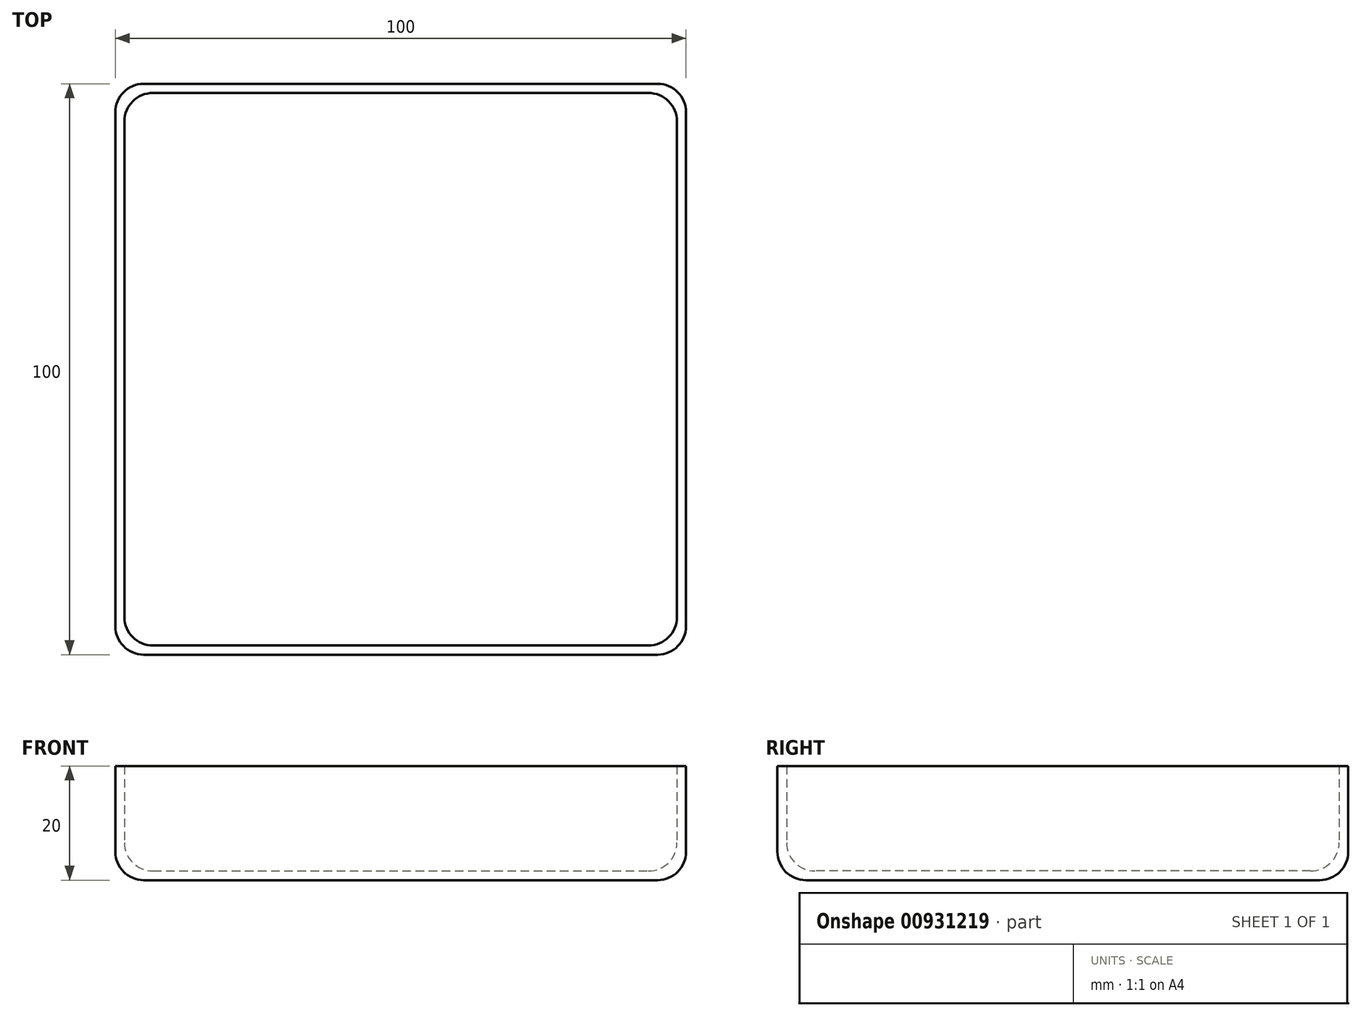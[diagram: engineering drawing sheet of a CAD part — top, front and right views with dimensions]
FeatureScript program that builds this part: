
annotation { "Feature Type Name" : "Feature", "Feature Type Description" : "" }
export const myFeature = defineFeature(function(context is Context, id is Id, definition is map)
    precondition{}
    {
        {
            var Q0;
            Q0=qCreatedBy(makeId("Top.planeOp"),FACE);
            var sketch = newSketch(context, id + "F0", { "sketchPlane" : qUnion([Q0])});
            skLineSegment(sketch, "E0.bottom", {"start": v(-50, 50) * mm, "end": v(50, 50) * mm});
            skLineSegment(sketch, "E0.top", {"start": v(-50, -50) * mm, "end": v(50, -50) * mm});
            skLineSegment(sketch, "E0.left", {"start": v(-50, 50) * mm, "end": v(-50, -50) * mm});
            skLineSegment(sketch, "E0.right", {"start": v(50, 50) * mm, "end": v(50, -50) * mm});
            skPoint(sketch, "E0.middle", {"position": v(0, 0) * mm});
            skSolve(sketch);
        }
        {
            var Q0;
            Q0 = qSketchRegion(id + "F0", true);
            extrude(context, id + "F1", {"entities" : qUnion([Q0]), "depth" : 20 * mm, "offsetDistance" : 25 * mm});
        }
        {
            var Q0;
            Q0=makeQuery(id+"F1.opExtrude","CAP_FACE",FACE,{"disambiguationData":[OSD([sQuery(id+"F0.wireOp",EDGE,"E0.bottom"),sQuery(id+"F0.wireOp",EDGE,"E0.top"),sQuery(id+"F0.wireOp",EDGE,"E0.left"),sQuery(id+"F0.wireOp",EDGE,"E0.right")])],"isStart":false});
            shell(context, id + "F2", {"entities" : qUnion([Q0]), "thickness" : 1.6 * mm});
        }
        {
            var Q0;
            {var subQ0=sQuery(id+"F0.wireOp",EDGE,"E0.left");Q0=makeQuery(id+"F2.opShell","OFFSET_EDGE",EDGE,{"disambiguationData":[OSD([subQ0]),TDD([makeQuery(id+"F1.opExtrude","CAP_EDGE",EDGE,{"disambiguationData":[OSD([subQ0])],"isStart":true})])]});}
            var Q1;
            {var subQ0=sQuery(id+"F0.wireOp",EDGE,"E0.bottom");Q1=makeQuery(id+"F2.opShell","OFFSET_EDGE",EDGE,{"disambiguationData":[OSD([subQ0]),TDD([makeQuery(id+"F1.opExtrude","CAP_EDGE",EDGE,{"disambiguationData":[OSD([subQ0])],"isStart":true})])]});}
            var Q2;
            {var subQ0=sQuery(id+"F0.wireOp",EDGE,"E0.right");Q2=makeQuery(id+"F2.opShell","OFFSET_EDGE",EDGE,{"disambiguationData":[OSD([subQ0]),TDD([makeQuery(id+"F1.opExtrude","CAP_EDGE",EDGE,{"disambiguationData":[OSD([subQ0])],"isStart":true})])]});}
            var Q3;
            {var subQ0=sQuery(id+"F0.wireOp",EDGE,"E0.top");Q3=makeQuery(id+"F2.opShell","OFFSET_EDGE",EDGE,{"disambiguationData":[OSD([subQ0]),TDD([makeQuery(id+"F1.opExtrude","CAP_EDGE",EDGE,{"disambiguationData":[OSD([subQ0])],"isStart":true})])]});}
            fillet(context, id + "F3", {"entities" : qUnion([Q0, Q1, Q2, Q3]), "radius" : 5 * mm, "tangentPropagation" : true, "allowEdgeOverflow" : false});
        }
        {
            var Q0;
            Q0=makeQuery(id+"F2.opShell","OFFSET_EDGE",EDGE,{"disambiguationData":[OSD([sQuery(id+"F0.wireOp",EDGE,"E0.bottom"),sQuery(id+"F0.wireOp",EDGE,"E0.right")])]});
            var Q1;
            {var subQ0=sQuery(id+"F0.wireOp",EDGE,"E0.right");var subQ1=sQuery(id+"F0.wireOp",EDGE,"E0.bottom");Q1=makeQuery(id+"F3.opFillet","BLEND_EDGE",EDGE,{"blendedFrom":[makeQuery(id+"F2.opShell","OFFSET_EDGE",EDGE,{"disambiguationData":[OSD([subQ1]),TDD([makeQuery(id+"F1.opExtrude","CAP_EDGE",EDGE,{"disambiguationData":[OSD([subQ1])],"isStart":true})])]}),makeQuery(id+"F2.opShell","OFFSET_EDGE",EDGE,{"disambiguationData":[OSD([subQ0]),TDD([makeQuery(id+"F1.opExtrude","CAP_EDGE",EDGE,{"disambiguationData":[OSD([subQ0])],"isStart":true})])]})],"blendedInto":[]});}
            var Q2;
            {var subQ0=sQuery(id+"F0.wireOp",EDGE,"E0.right");var subQ1=sQuery(id+"F0.wireOp",EDGE,"E0.top");Q2=makeQuery(id+"F3.opFillet","BLEND_EDGE",EDGE,{"blendedFrom":[makeQuery(id+"F2.opShell","OFFSET_EDGE",EDGE,{"disambiguationData":[OSD([subQ1]),TDD([makeQuery(id+"F1.opExtrude","CAP_EDGE",EDGE,{"disambiguationData":[OSD([subQ1])],"isStart":true})])]}),makeQuery(id+"F2.opShell","OFFSET_EDGE",EDGE,{"disambiguationData":[OSD([subQ0]),TDD([makeQuery(id+"F1.opExtrude","CAP_EDGE",EDGE,{"disambiguationData":[OSD([subQ0])],"isStart":true})])]})],"blendedInto":[]});}
            var Q3;
            Q3=makeQuery(id+"F2.opShell","OFFSET_EDGE",EDGE,{"disambiguationData":[OSD([sQuery(id+"F0.wireOp",EDGE,"E0.top"),sQuery(id+"F0.wireOp",EDGE,"E0.right")])]});
            var Q4;
            {var subQ0=sQuery(id+"F0.wireOp",EDGE,"E0.left");var subQ1=sQuery(id+"F0.wireOp",EDGE,"E0.top");Q4=makeQuery(id+"F3.opFillet","BLEND_EDGE",EDGE,{"blendedFrom":[makeQuery(id+"F2.opShell","OFFSET_EDGE",EDGE,{"disambiguationData":[OSD([subQ1]),TDD([makeQuery(id+"F1.opExtrude","CAP_EDGE",EDGE,{"disambiguationData":[OSD([subQ1])],"isStart":true})])]}),makeQuery(id+"F2.opShell","OFFSET_EDGE",EDGE,{"disambiguationData":[OSD([subQ0]),TDD([makeQuery(id+"F1.opExtrude","CAP_EDGE",EDGE,{"disambiguationData":[OSD([subQ0])],"isStart":true})])]})],"blendedInto":[]});}
            var Q5;
            Q5=makeQuery(id+"F2.opShell","OFFSET_EDGE",EDGE,{"disambiguationData":[OSD([sQuery(id+"F0.wireOp",EDGE,"E0.top"),sQuery(id+"F0.wireOp",EDGE,"E0.left")])]});
            var Q6;
            Q6=makeQuery(id+"F2.opShell","OFFSET_EDGE",EDGE,{"disambiguationData":[OSD([sQuery(id+"F0.wireOp",EDGE,"E0.bottom"),sQuery(id+"F0.wireOp",EDGE,"E0.left")])]});
            var Q7;
            {var subQ0=sQuery(id+"F0.wireOp",EDGE,"E0.left");var subQ1=sQuery(id+"F0.wireOp",EDGE,"E0.bottom");Q7=makeQuery(id+"F3.opFillet","BLEND_EDGE",EDGE,{"blendedFrom":[makeQuery(id+"F2.opShell","OFFSET_EDGE",EDGE,{"disambiguationData":[OSD([subQ1]),TDD([makeQuery(id+"F1.opExtrude","CAP_EDGE",EDGE,{"disambiguationData":[OSD([subQ1])],"isStart":true})])]}),makeQuery(id+"F2.opShell","OFFSET_EDGE",EDGE,{"disambiguationData":[OSD([subQ0]),TDD([makeQuery(id+"F1.opExtrude","CAP_EDGE",EDGE,{"disambiguationData":[OSD([subQ0])],"isStart":true})])]})],"blendedInto":[]});}
            fillet(context, id + "F4", {"entities" : qUnion([Q0, Q1, Q2, Q3, Q4, Q5, Q6, Q7]), "radius" : 5 * mm, "tangentPropagation" : true, "allowEdgeOverflow" : false});
        }
        {
            var Q0;
            Q0=makeQuery(id+"F1.opExtrude","SWEPT_EDGE",EDGE,{"disambiguationData":[OSD([sQuery(id+"F0.wireOp",EDGE,"E0.top"),sQuery(id+"F0.wireOp",EDGE,"E0.right")])]});
            var Q1;
            Q1=makeQuery(id+"F1.opExtrude","SWEPT_EDGE",EDGE,{"disambiguationData":[OSD([sQuery(id+"F0.wireOp",EDGE,"E0.top"),sQuery(id+"F0.wireOp",EDGE,"E0.left")])]});
            var Q2;
            Q2=makeQuery(id+"F1.opExtrude","SWEPT_EDGE",EDGE,{"disambiguationData":[OSD([sQuery(id+"F0.wireOp",EDGE,"E0.bottom"),sQuery(id+"F0.wireOp",EDGE,"E0.left")])]});
            var Q3;
            Q3=makeQuery(id+"F1.opExtrude","SWEPT_EDGE",EDGE,{"disambiguationData":[OSD([sQuery(id+"F0.wireOp",EDGE,"E0.bottom"),sQuery(id+"F0.wireOp",EDGE,"E0.right")])]});
            fillet(context, id + "F5", {"entities" : qUnion([Q0, Q1, Q2, Q3]), "radius" : 5 * mm, "tangentPropagation" : true, "allowEdgeOverflow" : false});
        }
        {
            var Q0;
            Q0=makeQuery(id+"F1.opExtrude","CAP_EDGE",EDGE,{"disambiguationData":[OSD([sQuery(id+"F0.wireOp",EDGE,"E0.left")])],"isStart":true});
            var Q1;
            Q1=makeQuery(id+"F1.opExtrude","CAP_EDGE",EDGE,{"disambiguationData":[OSD([sQuery(id+"F0.wireOp",EDGE,"E0.bottom")])],"isStart":true});
            var Q2;
            {var subQ0=sQuery(id+"F0.wireOp",EDGE,"E0.left");var subQ1=sQuery(id+"F0.wireOp",EDGE,"E0.bottom");Q2=makeQuery(id+"F5.opFillet","BLEND_EDGE",EDGE,{"blendedFrom":[makeQuery(id+"F1.opExtrude","SWEPT_EDGE",EDGE,{"disambiguationData":[OSD([subQ1,subQ0])]}),makeQuery(id+"F1.opExtrude","CAP_FACE",FACE,{"disambiguationData":[OSD([subQ1,sQuery(id+"F0.wireOp",EDGE,"E0.top"),subQ0,sQuery(id+"F0.wireOp",EDGE,"E0.right")])],"isStart":true})],"blendedInto":[makeQuery(id+"F1.opExtrude","CAP_FACE",FACE,{"disambiguationData":[OSD([subQ1,sQuery(id+"F0.wireOp",EDGE,"E0.top"),subQ0,sQuery(id+"F0.wireOp",EDGE,"E0.right")])],"isStart":true})]});}
            var Q3;
            {var subQ0=sQuery(id+"F0.wireOp",EDGE,"E0.right");var subQ1=sQuery(id+"F0.wireOp",EDGE,"E0.bottom");Q3=makeQuery(id+"F5.opFillet","BLEND_EDGE",EDGE,{"blendedFrom":[makeQuery(id+"F1.opExtrude","SWEPT_EDGE",EDGE,{"disambiguationData":[OSD([subQ1,subQ0])]}),makeQuery(id+"F1.opExtrude","CAP_FACE",FACE,{"disambiguationData":[OSD([subQ1,sQuery(id+"F0.wireOp",EDGE,"E0.top"),sQuery(id+"F0.wireOp",EDGE,"E0.left"),subQ0])],"isStart":true})],"blendedInto":[makeQuery(id+"F1.opExtrude","CAP_FACE",FACE,{"disambiguationData":[OSD([subQ1,sQuery(id+"F0.wireOp",EDGE,"E0.top"),sQuery(id+"F0.wireOp",EDGE,"E0.left"),subQ0])],"isStart":true})]});}
            var Q4;
            Q4=makeQuery(id+"F1.opExtrude","CAP_EDGE",EDGE,{"disambiguationData":[OSD([sQuery(id+"F0.wireOp",EDGE,"E0.right")])],"isStart":true});
            var Q5;
            {var subQ0=sQuery(id+"F0.wireOp",EDGE,"E0.right");var subQ1=sQuery(id+"F0.wireOp",EDGE,"E0.top");Q5=makeQuery(id+"F5.opFillet","BLEND_EDGE",EDGE,{"blendedFrom":[makeQuery(id+"F1.opExtrude","SWEPT_EDGE",EDGE,{"disambiguationData":[OSD([subQ1,subQ0])]}),makeQuery(id+"F1.opExtrude","CAP_FACE",FACE,{"disambiguationData":[OSD([sQuery(id+"F0.wireOp",EDGE,"E0.bottom"),subQ1,sQuery(id+"F0.wireOp",EDGE,"E0.left"),subQ0])],"isStart":true})],"blendedInto":[makeQuery(id+"F1.opExtrude","CAP_FACE",FACE,{"disambiguationData":[OSD([sQuery(id+"F0.wireOp",EDGE,"E0.bottom"),subQ1,sQuery(id+"F0.wireOp",EDGE,"E0.left"),subQ0])],"isStart":true})]});}
            var Q6;
            Q6=makeQuery(id+"F1.opExtrude","CAP_EDGE",EDGE,{"disambiguationData":[OSD([sQuery(id+"F0.wireOp",EDGE,"E0.top")])],"isStart":true});
            var Q7;
            {var subQ0=sQuery(id+"F0.wireOp",EDGE,"E0.left");var subQ1=sQuery(id+"F0.wireOp",EDGE,"E0.top");Q7=makeQuery(id+"F5.opFillet","BLEND_EDGE",EDGE,{"blendedFrom":[makeQuery(id+"F1.opExtrude","SWEPT_EDGE",EDGE,{"disambiguationData":[OSD([subQ1,subQ0])]}),makeQuery(id+"F1.opExtrude","CAP_FACE",FACE,{"disambiguationData":[OSD([sQuery(id+"F0.wireOp",EDGE,"E0.bottom"),subQ1,subQ0,sQuery(id+"F0.wireOp",EDGE,"E0.right")])],"isStart":true})],"blendedInto":[makeQuery(id+"F1.opExtrude","CAP_FACE",FACE,{"disambiguationData":[OSD([sQuery(id+"F0.wireOp",EDGE,"E0.bottom"),subQ1,subQ0,sQuery(id+"F0.wireOp",EDGE,"E0.right")])],"isStart":true})]});}
            fillet(context, id + "F6", {"entities" : qUnion([Q0, Q1, Q2, Q3, Q4, Q5, Q6, Q7]), "radius" : 5 * mm, "tangentPropagation" : true, "allowEdgeOverflow" : false});
        }
    });
